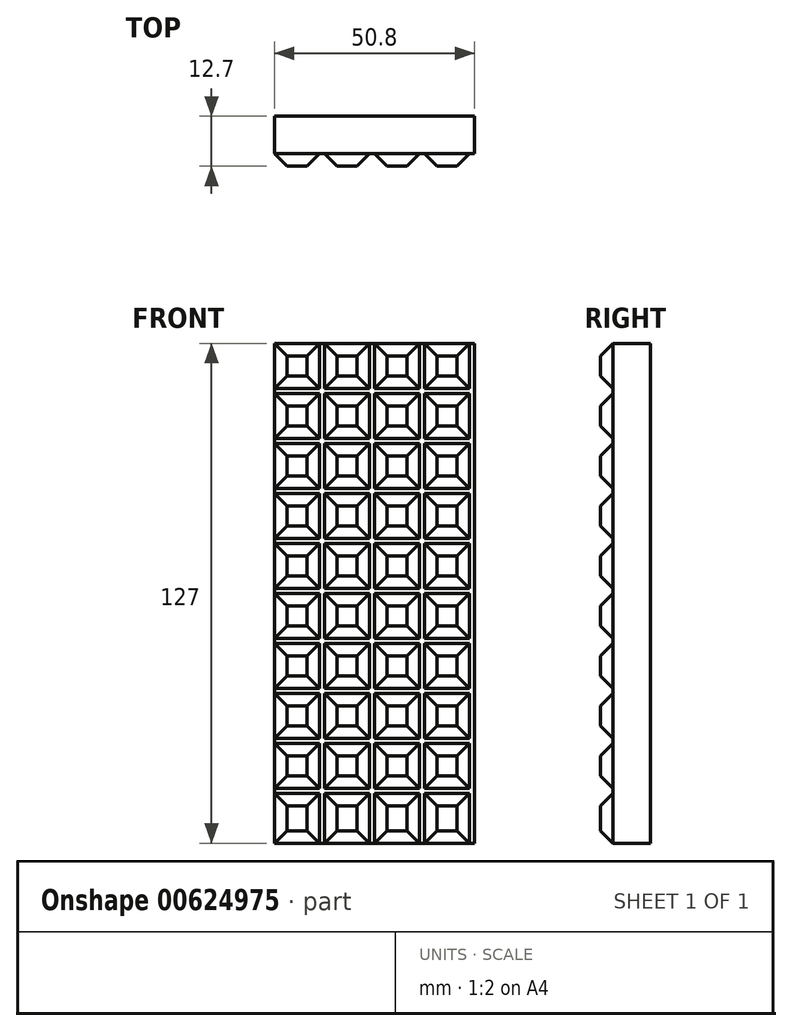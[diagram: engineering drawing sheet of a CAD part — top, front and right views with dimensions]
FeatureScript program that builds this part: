
annotation { "Feature Type Name" : "Feature", "Feature Type Description" : "" }
export const myFeature = defineFeature(function(context is Context, id is Id, definition is map)
    precondition{}
    {
        {
            var Q0;
            Q0=qCreatedBy(makeId("Front.planeOp"),FACE);
            var sketch = newSketch(context, id + "F0", { "sketchPlane" : qUnion([Q0])});
            skLineSegment(sketch, "E0.bottom", {"start": v(0, 0) * mm, "end": v(50.8, 0) * mm});
            skLineSegment(sketch, "E0.top", {"start": v(0, 127) * mm, "end": v(50.8, 127) * mm});
            skLineSegment(sketch, "E0.left", {"start": v(0, 0) * mm, "end": v(0, 127) * mm});
            skLineSegment(sketch, "E0.right", {"start": v(50.8, 0) * mm, "end": v(50.8, 127) * mm});
            skSolve(sketch);
        }
        {
            var Q0;
            Q0 = qSketchRegion(id + "F0", true);
            extrude(context, id + "F1", {"entities" : qUnion([Q0]), "depth" : 12.7 * mm, "offsetDistance" : 25.4 * mm});
        }
        {
            var Q0;
            Q0=makeQuery(id+"F1.opExtrude","CAP_FACE",FACE,{"disambiguationData":[OSD([sQuery(id+"F0.wireOp",EDGE,"E0.bottom"),sQuery(id+"F0.wireOp",EDGE,"E0.top"),sQuery(id+"F0.wireOp",EDGE,"E0.left"),sQuery(id+"F0.wireOp",EDGE,"E0.right")])],"isStart":false});
            var sketch = newSketch(context, id + "F2", { "sketchPlane" : qUnion([Q0])});
            skLineSegment(sketch, "E1", {"start": v(11.43, 0) * mm, "end": v(11.43, 12.7) * mm});
            skLineSegment(sketch, "E2", {"start": v(12.7, 127) * mm, "end": v(12.7, 115.57) * mm});
            skLineSegment(sketch, "E3.1.0.0", {"start": v(25.4, 127) * mm, "end": v(25.4, 115.57) * mm});
            skLineSegment(sketch, "E3.1.0.1", {"start": v(24.13, 0) * mm, "end": v(24.13, 12.7) * mm});
            skLineSegment(sketch, "E3.2.0.0", {"start": v(38.1, 127) * mm, "end": v(38.1, 115.57) * mm});
            skLineSegment(sketch, "E3.2.0.1", {"start": v(36.83, 0) * mm, "end": v(36.83, 12.7) * mm});
            skLineSegment(sketch, "E3.direction1", {"start": v(11.43, 0) * mm, "end": v(24.13, 0) * mm, "construction": true});
            skLineSegment(sketch, "E4.0.3.0", {"start": v(50.8, 127) * mm, "end": v(50.8, 0) * mm});
            skLineSegment(sketch, "E4.3.3.0", {"start": v(49.53, 0) * mm, "end": v(49.53, 12.7) * mm});
            skLineSegment(sketch, "E5", {"start": v(0, 115.57) * mm, "end": v(11.43, 115.57) * mm});
            skLineSegment(sketch, "E6", {"start": v(0, 114.3) * mm, "end": v(11.43, 114.3) * mm});
            skLineSegment(sketch, "E7.0.1.0", {"start": v(0, 101.6) * mm, "end": v(11.43, 101.6) * mm});
            skLineSegment(sketch, "E7.0.1.1", {"start": v(0, 102.87) * mm, "end": v(11.43, 102.87) * mm});
            skLineSegment(sketch, "E7.0.2.0", {"start": v(0, 88.9) * mm, "end": v(11.43, 88.9) * mm});
            skLineSegment(sketch, "E7.0.2.1", {"start": v(0, 90.17) * mm, "end": v(11.43, 90.17) * mm});
            skLineSegment(sketch, "E7.0.3.0", {"start": v(0, 76.2) * mm, "end": v(11.43, 76.2) * mm});
            skLineSegment(sketch, "E7.0.3.1", {"start": v(0, 77.47) * mm, "end": v(11.43, 77.47) * mm});
            skLineSegment(sketch, "E7.0.4.0", {"start": v(0, 63.5) * mm, "end": v(11.43, 63.5) * mm});
            skLineSegment(sketch, "E7.0.4.1", {"start": v(0, 64.77) * mm, "end": v(11.43, 64.77) * mm});
            skLineSegment(sketch, "E7.0.5.0", {"start": v(0, 50.8) * mm, "end": v(11.43, 50.8) * mm});
            skLineSegment(sketch, "E7.0.5.1", {"start": v(0, 52.07) * mm, "end": v(11.43, 52.07) * mm});
            skLineSegment(sketch, "E7.0.6.0", {"start": v(0, 38.1) * mm, "end": v(11.43, 38.1) * mm});
            skLineSegment(sketch, "E7.0.6.1", {"start": v(0, 39.37) * mm, "end": v(11.43, 39.37) * mm});
            skLineSegment(sketch, "E7.0.7.0", {"start": v(0, 25.4) * mm, "end": v(11.43, 25.4) * mm});
            skLineSegment(sketch, "E7.0.7.1", {"start": v(0, 26.67) * mm, "end": v(11.43, 26.67) * mm});
            skLineSegment(sketch, "E7.0.8.0", {"start": v(0, 12.7) * mm, "end": v(11.43, 12.7) * mm});
            skLineSegment(sketch, "E7.0.8.1", {"start": v(0, 13.97) * mm, "end": v(11.43, 13.97) * mm});
            skLineSegment(sketch, "E7.0.9.0", {"start": v(0, 0) * mm, "end": v(50.8, 0) * mm});
            skLineSegment(sketch, "E7.direction1", {"start": v(0, 114.3) * mm, "end": v(-26.1, 114.3) * mm, "construction": true});
            skLineSegment(sketch, "E7.direction2", {"start": v(0, 114.3) * mm, "end": v(0, 101.6) * mm, "construction": true});
            skLineSegment(sketch, "E8", {"start": v(0, 127) * mm, "end": v(0, -127) * mm});
            skLineSegment(sketch, "E9", {"start": v(0, 127) * mm, "end": v(101.6, 127) * mm});
            skLineSegment(sketch, "E10.trimOffspring", {"start": v(12.7, 115.57) * mm, "end": v(24.13, 115.57) * mm});
            skLineSegment(sketch, "E11.trimOffspring", {"start": v(12.7, 114.3) * mm, "end": v(12.7, 102.87) * mm});
            skLineSegment(sketch, "E12.trimOffspring", {"start": v(12.7, 114.3) * mm, "end": v(24.13, 114.3) * mm});
            skLineSegment(sketch, "E13.trimOffspring", {"start": v(11.43, 115.57) * mm, "end": v(11.43, 127) * mm});
            skLineSegment(sketch, "E14.trimOffspring", {"start": v(24.13, 115.57) * mm, "end": v(24.13, 127) * mm});
            skLineSegment(sketch, "E15.trimOffspring", {"start": v(25.4, 115.57) * mm, "end": v(36.83, 115.57) * mm});
            skLineSegment(sketch, "E16.trimOffspring", {"start": v(25.4, 114.3) * mm, "end": v(25.4, 102.87) * mm});
            skLineSegment(sketch, "E17.trimOffspring", {"start": v(25.4, 114.3) * mm, "end": v(36.83, 114.3) * mm});
            skLineSegment(sketch, "E18.trimOffspring", {"start": v(38.1, 115.57) * mm, "end": v(49.53, 115.57) * mm});
            skLineSegment(sketch, "E19.trimOffspring", {"start": v(38.1, 114.3) * mm, "end": v(38.1, 102.87) * mm});
            skLineSegment(sketch, "E20.trimOffspring", {"start": v(38.1, 114.3) * mm, "end": v(49.53, 114.3) * mm});
            skLineSegment(sketch, "E21.trimOffspring", {"start": v(36.83, 115.57) * mm, "end": v(36.83, 127) * mm});
            skLineSegment(sketch, "E22.trimOffspring", {"start": v(49.53, 115.57) * mm, "end": v(49.53, 127) * mm});
            skPoint(sketch, "E23.orphan", {"position": v(50.8, 115.57) * mm});
            skPoint(sketch, "E24.orphan", {"position": v(50.8, 114.3) * mm});
            skPoint(sketch, "E25.orphan", {"position": v(50.8, 102.87) * mm});
            skLineSegment(sketch, "E26.trimOffspring", {"start": v(49.53, 102.87) * mm, "end": v(49.53, 114.3) * mm});
            skPoint(sketch, "E27.orphan", {"position": v(50.8, 101.6) * mm});
            skLineSegment(sketch, "E28.trimOffspring", {"start": v(38.1, 101.6) * mm, "end": v(38.1, 90.17) * mm});
            skLineSegment(sketch, "E29.trimOffspring", {"start": v(38.1, 102.87) * mm, "end": v(49.53, 102.87) * mm});
            skLineSegment(sketch, "E30.trimOffspring", {"start": v(36.83, 102.87) * mm, "end": v(36.83, 114.3) * mm});
            skLineSegment(sketch, "E31.trimOffspring", {"start": v(38.1, 101.6) * mm, "end": v(49.53, 101.6) * mm});
            skLineSegment(sketch, "E32.trimOffspring", {"start": v(25.4, 101.6) * mm, "end": v(25.4, 90.17) * mm});
            skLineSegment(sketch, "E33.trimOffspring", {"start": v(25.4, 102.87) * mm, "end": v(36.83, 102.87) * mm});
            skLineSegment(sketch, "E34.trimOffspring", {"start": v(24.13, 102.87) * mm, "end": v(24.13, 114.3) * mm});
            skLineSegment(sketch, "E35.trimOffspring", {"start": v(25.4, 101.6) * mm, "end": v(36.83, 101.6) * mm});
            skLineSegment(sketch, "E36.trimOffspring", {"start": v(12.7, 102.87) * mm, "end": v(24.13, 102.87) * mm});
            skLineSegment(sketch, "E37.trimOffspring", {"start": v(11.43, 102.87) * mm, "end": v(11.43, 114.3) * mm});
            skLineSegment(sketch, "E38.trimOffspring", {"start": v(12.7, 101.6) * mm, "end": v(24.13, 101.6) * mm});
            skLineSegment(sketch, "E39.trimOffspring", {"start": v(11.43, 90.17) * mm, "end": v(11.43, 101.6) * mm});
            skLineSegment(sketch, "E40.trimOffspring", {"start": v(12.7, 90.17) * mm, "end": v(24.13, 90.17) * mm});
            skLineSegment(sketch, "E41.trimOffspring", {"start": v(12.7, 88.9) * mm, "end": v(24.13, 88.9) * mm});
            skLineSegment(sketch, "E42.trimOffspring", {"start": v(12.7, 88.9) * mm, "end": v(12.7, 77.47) * mm});
            skLineSegment(sketch, "E43.trimOffspring", {"start": v(24.13, 90.17) * mm, "end": v(24.13, 101.6) * mm});
            skLineSegment(sketch, "E44.trimOffspring", {"start": v(25.4, 90.17) * mm, "end": v(36.83, 90.17) * mm});
            skLineSegment(sketch, "E45.trimOffspring", {"start": v(25.4, 88.9) * mm, "end": v(25.4, 77.47) * mm});
            skLineSegment(sketch, "E46.trimOffspring", {"start": v(25.4, 88.9) * mm, "end": v(36.83, 88.9) * mm});
            skLineSegment(sketch, "E47.trimOffspring", {"start": v(36.83, 90.17) * mm, "end": v(36.83, 101.6) * mm});
            skLineSegment(sketch, "E48.trimOffspring", {"start": v(38.1, 90.17) * mm, "end": v(49.53, 90.17) * mm});
            skLineSegment(sketch, "E49.trimOffspring", {"start": v(38.1, 88.9) * mm, "end": v(38.1, 77.47) * mm});
            skLineSegment(sketch, "E50.trimOffspring", {"start": v(38.1, 88.9) * mm, "end": v(49.53, 88.9) * mm});
            skLineSegment(sketch, "E51.trimOffspring", {"start": v(49.53, 90.17) * mm, "end": v(49.53, 101.6) * mm});
            skPoint(sketch, "E52.orphan", {"position": v(50.8, 90.17) * mm});
            skPoint(sketch, "E53.orphan", {"position": v(50.8, 88.9) * mm});
            skPoint(sketch, "E54.orphan", {"position": v(50.8, 77.47) * mm});
            skLineSegment(sketch, "E55.trimOffspring", {"start": v(49.53, 77.47) * mm, "end": v(49.53, 88.9) * mm});
            skPoint(sketch, "E56.orphan", {"position": v(50.8, 76.2) * mm});
            skLineSegment(sketch, "E57.trimOffspring", {"start": v(38.1, 76.2) * mm, "end": v(38.1, 64.77) * mm});
            skLineSegment(sketch, "E58.trimOffspring", {"start": v(38.1, 77.47) * mm, "end": v(49.53, 77.47) * mm});
            skLineSegment(sketch, "E59.trimOffspring", {"start": v(36.83, 77.47) * mm, "end": v(36.83, 88.9) * mm});
            skLineSegment(sketch, "E60.trimOffspring", {"start": v(38.1, 76.2) * mm, "end": v(49.53, 76.2) * mm});
            skLineSegment(sketch, "E61.trimOffspring", {"start": v(25.4, 76.2) * mm, "end": v(25.4, 64.77) * mm});
            skLineSegment(sketch, "E62.trimOffspring", {"start": v(25.4, 77.47) * mm, "end": v(36.83, 77.47) * mm});
            skLineSegment(sketch, "E63.trimOffspring", {"start": v(24.13, 77.47) * mm, "end": v(24.13, 88.9) * mm});
            skLineSegment(sketch, "E64.trimOffspring", {"start": v(25.4, 76.2) * mm, "end": v(36.83, 76.2) * mm});
            skLineSegment(sketch, "E65.trimOffspring", {"start": v(12.7, 76.2) * mm, "end": v(12.7, 64.77) * mm});
            skLineSegment(sketch, "E66.trimOffspring", {"start": v(11.43, 77.47) * mm, "end": v(11.43, 88.9) * mm});
            skLineSegment(sketch, "E67.trimOffspring", {"start": v(12.7, 77.47) * mm, "end": v(24.13, 77.47) * mm});
            skLineSegment(sketch, "E68.trimOffspring", {"start": v(12.7, 76.2) * mm, "end": v(24.13, 76.2) * mm});
            skLineSegment(sketch, "E69.trimOffspring", {"start": v(12.7, 64.77) * mm, "end": v(24.13, 64.77) * mm});
            skLineSegment(sketch, "E70.trimOffspring", {"start": v(12.7, 63.5) * mm, "end": v(12.7, 52.07) * mm});
            skLineSegment(sketch, "E71.trimOffspring", {"start": v(12.7, 63.5) * mm, "end": v(24.13, 63.5) * mm});
            skLineSegment(sketch, "E72.trimOffspring", {"start": v(11.43, 64.77) * mm, "end": v(11.43, 76.2) * mm});
            skLineSegment(sketch, "E73.trimOffspring", {"start": v(24.13, 64.77) * mm, "end": v(24.13, 76.2) * mm});
            skLineSegment(sketch, "E74.trimOffspring", {"start": v(25.4, 64.77) * mm, "end": v(36.83, 64.77) * mm});
            skLineSegment(sketch, "E75.trimOffspring", {"start": v(25.4, 63.5) * mm, "end": v(25.4, 52.07) * mm});
            skLineSegment(sketch, "E76.trimOffspring", {"start": v(25.4, 63.5) * mm, "end": v(36.83, 63.5) * mm});
            skLineSegment(sketch, "E77.trimOffspring", {"start": v(36.83, 64.77) * mm, "end": v(36.83, 76.2) * mm});
            skLineSegment(sketch, "E78.trimOffspring", {"start": v(38.1, 64.77) * mm, "end": v(49.53, 64.77) * mm});
            skLineSegment(sketch, "E79.trimOffspring", {"start": v(38.1, 63.5) * mm, "end": v(38.1, 52.07) * mm});
            skLineSegment(sketch, "E80.trimOffspring", {"start": v(38.1, 63.5) * mm, "end": v(49.53, 63.5) * mm});
            skLineSegment(sketch, "E81.trimOffspring", {"start": v(49.53, 64.77) * mm, "end": v(49.53, 76.2) * mm});
            skPoint(sketch, "E82.orphan", {"position": v(50.8, 64.77) * mm});
            skPoint(sketch, "E83.orphan", {"position": v(50.8, 63.5) * mm});
            skPoint(sketch, "E84.orphan", {"position": v(50.8, 52.07) * mm});
            skLineSegment(sketch, "E85.trimOffspring", {"start": v(49.53, 52.07) * mm, "end": v(49.53, 63.5) * mm});
            skPoint(sketch, "E86.orphan", {"position": v(50.8, 50.8) * mm});
            skLineSegment(sketch, "E87.trimOffspring", {"start": v(38.1, 50.8) * mm, "end": v(38.1, 39.37) * mm});
            skLineSegment(sketch, "E88.trimOffspring", {"start": v(38.1, 52.07) * mm, "end": v(49.53, 52.07) * mm});
            skLineSegment(sketch, "E89.trimOffspring", {"start": v(36.83, 52.07) * mm, "end": v(36.83, 63.5) * mm});
            skLineSegment(sketch, "E90.trimOffspring", {"start": v(38.1, 50.8) * mm, "end": v(49.53, 50.8) * mm});
            skLineSegment(sketch, "E91.trimOffspring", {"start": v(25.4, 50.8) * mm, "end": v(25.4, 39.37) * mm});
            skLineSegment(sketch, "E92.trimOffspring", {"start": v(25.4, 52.07) * mm, "end": v(36.83, 52.07) * mm});
            skLineSegment(sketch, "E93.trimOffspring", {"start": v(24.13, 52.07) * mm, "end": v(24.13, 63.5) * mm});
            skLineSegment(sketch, "E94.trimOffspring", {"start": v(25.4, 50.8) * mm, "end": v(36.83, 50.8) * mm});
            skLineSegment(sketch, "E95.trimOffspring", {"start": v(12.7, 50.8) * mm, "end": v(12.7, 39.37) * mm});
            skLineSegment(sketch, "E96.trimOffspring", {"start": v(12.7, 52.07) * mm, "end": v(24.13, 52.07) * mm});
            skLineSegment(sketch, "E97.trimOffspring", {"start": v(11.43, 52.07) * mm, "end": v(11.43, 63.5) * mm});
            skLineSegment(sketch, "E98.trimOffspring", {"start": v(12.7, 50.8) * mm, "end": v(24.13, 50.8) * mm});
            skLineSegment(sketch, "E99.trimOffspring", {"start": v(12.7, 39.37) * mm, "end": v(24.13, 39.37) * mm});
            skLineSegment(sketch, "E100.trimOffspring", {"start": v(12.7, 38.1) * mm, "end": v(12.7, 26.67) * mm});
            skLineSegment(sketch, "E101.trimOffspring", {"start": v(12.7, 38.1) * mm, "end": v(24.13, 38.1) * mm});
            skLineSegment(sketch, "E102.trimOffspring", {"start": v(11.43, 39.37) * mm, "end": v(11.43, 50.8) * mm});
            skLineSegment(sketch, "E103.trimOffspring", {"start": v(24.13, 39.37) * mm, "end": v(24.13, 50.8) * mm});
            skLineSegment(sketch, "E104.trimOffspring", {"start": v(25.4, 39.37) * mm, "end": v(36.83, 39.37) * mm});
            skLineSegment(sketch, "E105.trimOffspring", {"start": v(25.4, 38.1) * mm, "end": v(25.4, 26.67) * mm});
            skLineSegment(sketch, "E106.trimOffspring", {"start": v(25.4, 38.1) * mm, "end": v(36.83, 38.1) * mm});
            skLineSegment(sketch, "E107.trimOffspring", {"start": v(36.83, 39.37) * mm, "end": v(36.83, 50.8) * mm});
            skLineSegment(sketch, "E108.trimOffspring", {"start": v(38.1, 39.37) * mm, "end": v(49.53, 39.37) * mm});
            skLineSegment(sketch, "E109.trimOffspring", {"start": v(38.1, 38.1) * mm, "end": v(38.1, 26.67) * mm});
            skLineSegment(sketch, "E110.trimOffspring", {"start": v(38.1, 38.1) * mm, "end": v(49.53, 38.1) * mm});
            skLineSegment(sketch, "E111.trimOffspring", {"start": v(49.53, 39.37) * mm, "end": v(49.53, 50.8) * mm});
            skPoint(sketch, "E112.orphan", {"position": v(50.8, 39.37) * mm});
            skPoint(sketch, "E113.orphan", {"position": v(50.8, 38.1) * mm});
            skPoint(sketch, "E114.orphan", {"position": v(50.8, 26.67) * mm});
            skPoint(sketch, "E115.orphan", {"position": v(50.8, 25.4) * mm});
            skLineSegment(sketch, "E116.trimOffspring", {"start": v(49.53, 26.67) * mm, "end": v(49.53, 38.1) * mm});
            skLineSegment(sketch, "E117.trimOffspring", {"start": v(38.1, 25.4) * mm, "end": v(38.1, 13.97) * mm});
            skLineSegment(sketch, "E118.trimOffspring", {"start": v(38.1, 26.67) * mm, "end": v(49.53, 26.67) * mm});
            skLineSegment(sketch, "E119.trimOffspring", {"start": v(36.83, 26.67) * mm, "end": v(36.83, 38.1) * mm});
            skLineSegment(sketch, "E120.trimOffspring", {"start": v(38.1, 25.4) * mm, "end": v(49.53, 25.4) * mm});
            skLineSegment(sketch, "E121.trimOffspring", {"start": v(25.4, 25.4) * mm, "end": v(25.4, 13.97) * mm});
            skLineSegment(sketch, "E122.trimOffspring", {"start": v(25.4, 26.67) * mm, "end": v(36.83, 26.67) * mm});
            skLineSegment(sketch, "E123.trimOffspring", {"start": v(24.13, 26.67) * mm, "end": v(24.13, 38.1) * mm});
            skLineSegment(sketch, "E124.trimOffspring", {"start": v(25.4, 25.4) * mm, "end": v(36.83, 25.4) * mm});
            skLineSegment(sketch, "E125.trimOffspring", {"start": v(12.7, 25.4) * mm, "end": v(12.7, 13.97) * mm});
            skLineSegment(sketch, "E126.trimOffspring", {"start": v(12.7, 26.67) * mm, "end": v(24.13, 26.67) * mm});
            skLineSegment(sketch, "E127.trimOffspring", {"start": v(11.43, 26.67) * mm, "end": v(11.43, 38.1) * mm});
            skLineSegment(sketch, "E128.trimOffspring", {"start": v(12.7, 25.4) * mm, "end": v(24.13, 25.4) * mm});
            skLineSegment(sketch, "E129.trimOffspring", {"start": v(12.7, 13.97) * mm, "end": v(24.13, 13.97) * mm});
            skLineSegment(sketch, "E130.trimOffspring", {"start": v(11.43, 13.97) * mm, "end": v(11.43, 25.4) * mm});
            skLineSegment(sketch, "E131.trimOffspring", {"start": v(12.7, 12.7) * mm, "end": v(12.7, 0) * mm});
            skLineSegment(sketch, "E132.trimOffspring", {"start": v(12.7, 12.7) * mm, "end": v(24.13, 12.7) * mm});
            skLineSegment(sketch, "E133.trimOffspring", {"start": v(24.13, 13.97) * mm, "end": v(24.13, 25.4) * mm});
            skLineSegment(sketch, "E134.trimOffspring", {"start": v(25.4, 13.97) * mm, "end": v(36.83, 13.97) * mm});
            skLineSegment(sketch, "E135.trimOffspring", {"start": v(25.4, 12.7) * mm, "end": v(25.4, 0) * mm});
            skLineSegment(sketch, "E136.trimOffspring", {"start": v(25.4, 12.7) * mm, "end": v(36.83, 12.7) * mm});
            skLineSegment(sketch, "E137.trimOffspring", {"start": v(36.83, 13.97) * mm, "end": v(36.83, 25.4) * mm});
            skLineSegment(sketch, "E138.trimOffspring", {"start": v(38.1, 13.97) * mm, "end": v(49.53, 13.97) * mm});
            skLineSegment(sketch, "E139.trimOffspring", {"start": v(38.1, 12.7) * mm, "end": v(38.1, 0) * mm});
            skLineSegment(sketch, "E140.trimOffspring", {"start": v(38.1, 12.7) * mm, "end": v(49.53, 12.7) * mm});
            skLineSegment(sketch, "E141.trimOffspring", {"start": v(49.53, 13.97) * mm, "end": v(49.53, 25.4) * mm});
            skPoint(sketch, "E142.orphan", {"position": v(50.8, 13.97) * mm});
            skPoint(sketch, "E143.orphan", {"position": v(50.8, 12.7) * mm});
            skPoint(sketch, "E144.orphan", {"position": v(50.8, 1.27) * mm});
            skLineSegment(sketch, "E145", {"start": v(12.7, 101.6) * mm, "end": v(12.7, 90.17) * mm});
            skSolve(sketch);
        }
        {
            var Q0;
            {var subQ23=sQuery(id+"F2.wireOp",EDGE,"E1");Q0=makeQuery(id+"F2.imprint","IMPRINT",FACE,{"disambiguationData":[TD([[makeQuery(id+"F2.imprint","IMPRINT",EDGE,{"derivedFrom":subQ23}),-1.0]])]});}
            extrude(context, id + "F3", {"entities" : qUnion([Q0]), "operationType" : NewBodyOperationType.REMOVE, "oppositeDirection" : true, "depth" : 3.17 * mm, "offsetDistance" : 25.4 * mm});
        }
        {
            var Q0;
            Q0=makeQuery(id+"F3.boolean.opBoolean","COPY",EDGE,{"derivedFrom":makeQuery(id+"F3.opExtrude","CAP_EDGE",EDGE,{"disambiguationData":[OSD([sQuery(id+"F2.wireOp",EDGE,"E1")])],"isStart":true})});
            var Q1;
            Q1=makeQuery(id+"F3.boolean.opBoolean","COPY",EDGE,{"derivedFrom":makeQuery(id+"F3.opExtrude","CAP_EDGE",EDGE,{"disambiguationData":[OSD([sQuery(id+"F2.wireOp",EDGE,"E7.0.8.0")])],"isStart":true})});
            var Q2;
            Q2=makeQuery(id+"F3.boolean.opBoolean","COPY",EDGE,{"derivedFrom":makeQuery(id+"F3.opExtrude","CAP_EDGE",EDGE,{"disambiguationData":[OSD([sQuery(id+"F2.wireOp",EDGE,"E132.trimOffspring")])],"isStart":true})});
            var Q3;
            Q3=makeQuery(id+"F3.boolean.opBoolean","COPY",EDGE,{"derivedFrom":makeQuery(id+"F3.opExtrude","CAP_EDGE",EDGE,{"disambiguationData":[OSD([sQuery(id+"F2.wireOp",EDGE,"E131.trimOffspring")])],"isStart":true})});
            var Q4;
            Q4=makeQuery(id+"F3.boolean.opBoolean","COPY",EDGE,{"derivedFrom":makeQuery(id+"F3.opExtrude","CAP_EDGE",EDGE,{"disambiguationData":[OSD([sQuery(id+"F2.wireOp",EDGE,"E3.1.0.1")])],"isStart":true})});
            var Q5;
            Q5=makeQuery(id+"F3.boolean.opBoolean","COPY",EDGE,{"derivedFrom":makeQuery(id+"F3.opExtrude","CAP_EDGE",EDGE,{"disambiguationData":[OSD([sQuery(id+"F2.wireOp",EDGE,"E136.trimOffspring")])],"isStart":true})});
            var Q6;
            Q6=makeQuery(id+"F3.boolean.opBoolean","COPY",EDGE,{"derivedFrom":makeQuery(id+"F3.opExtrude","CAP_EDGE",EDGE,{"disambiguationData":[OSD([sQuery(id+"F2.wireOp",EDGE,"E135.trimOffspring")])],"isStart":true})});
            var Q7;
            Q7=makeQuery(id+"F3.boolean.opBoolean","COPY",EDGE,{"derivedFrom":makeQuery(id+"F3.opExtrude","CAP_EDGE",EDGE,{"disambiguationData":[OSD([sQuery(id+"F2.wireOp",EDGE,"E3.2.0.1")])],"isStart":true})});
            var Q8;
            Q8=makeQuery(id+"F3.boolean.opBoolean","COPY",EDGE,{"derivedFrom":makeQuery(id+"F3.opExtrude","CAP_EDGE",EDGE,{"disambiguationData":[OSD([sQuery(id+"F2.wireOp",EDGE,"E139.trimOffspring")])],"isStart":true})});
            var Q9;
            Q9=makeQuery(id+"F3.boolean.opBoolean","COPY",EDGE,{"derivedFrom":makeQuery(id+"F3.opExtrude","CAP_EDGE",EDGE,{"disambiguationData":[OSD([sQuery(id+"F2.wireOp",EDGE,"E140.trimOffspring")])],"isStart":true})});
            var Q10;
            Q10=makeQuery(id+"F3.boolean.opBoolean","COPY",EDGE,{"derivedFrom":makeQuery(id+"F3.opExtrude","CAP_EDGE",EDGE,{"disambiguationData":[OSD([sQuery(id+"F2.wireOp",EDGE,"E138.trimOffspring")])],"isStart":true})});
            var Q11;
            Q11=makeQuery(id+"F3.boolean.opBoolean","COPY",EDGE,{"derivedFrom":makeQuery(id+"F3.opExtrude","CAP_EDGE",EDGE,{"disambiguationData":[OSD([sQuery(id+"F2.wireOp",EDGE,"E117.trimOffspring")])],"isStart":true})});
            var Q12;
            Q12=makeQuery(id+"F3.boolean.opBoolean","COPY",EDGE,{"derivedFrom":makeQuery(id+"F3.opExtrude","CAP_EDGE",EDGE,{"disambiguationData":[OSD([sQuery(id+"F2.wireOp",EDGE,"E120.trimOffspring")])],"isStart":true})});
            var Q13;
            Q13=makeQuery(id+"F3.boolean.opBoolean","COPY",EDGE,{"derivedFrom":makeQuery(id+"F3.opExtrude","CAP_EDGE",EDGE,{"disambiguationData":[OSD([sQuery(id+"F2.wireOp",EDGE,"E137.trimOffspring")])],"isStart":true})});
            var Q14;
            Q14=makeQuery(id+"F3.boolean.opBoolean","SPLIT",FACE,{"disambiguationData":[TD([makeQuery(id+"F3.opExtrude","SWEPT_FACE",FACE,{"disambiguationData":[OSD([sQuery(id+"F2.wireOp",EDGE,"E125.trimOffspring")])]})])],"derivedFrom":makeQuery(id+"F1.opExtrude","CAP_FACE",FACE,{"disambiguationData":[OSD([sQuery(id+"F0.wireOp",EDGE,"E0.bottom"),sQuery(id+"F0.wireOp",EDGE,"E0.top"),sQuery(id+"F0.wireOp",EDGE,"E0.left"),sQuery(id+"F0.wireOp",EDGE,"E0.right")])],"isStart":false})});
            var Q15;
            Q15=makeQuery(id+"F3.boolean.opBoolean","SPLIT",FACE,{"disambiguationData":[TD([makeQuery(id+"F3.opExtrude","SWEPT_FACE",FACE,{"disambiguationData":[OSD([sQuery(id+"F2.wireOp",EDGE,"E105.trimOffspring")])]})])],"derivedFrom":makeQuery(id+"F1.opExtrude","CAP_FACE",FACE,{"disambiguationData":[OSD([sQuery(id+"F0.wireOp",EDGE,"E0.bottom"),sQuery(id+"F0.wireOp",EDGE,"E0.top"),sQuery(id+"F0.wireOp",EDGE,"E0.left"),sQuery(id+"F0.wireOp",EDGE,"E0.right")])],"isStart":false})});
            var Q16;
            Q16=makeQuery(id+"F3.boolean.opBoolean","SPLIT",FACE,{"disambiguationData":[TD([makeQuery(id+"F3.opExtrude","SWEPT_FACE",FACE,{"disambiguationData":[OSD([sQuery(id+"F2.wireOp",EDGE,"E100.trimOffspring")])]})])],"derivedFrom":makeQuery(id+"F1.opExtrude","CAP_FACE",FACE,{"disambiguationData":[OSD([sQuery(id+"F0.wireOp",EDGE,"E0.bottom"),sQuery(id+"F0.wireOp",EDGE,"E0.top"),sQuery(id+"F0.wireOp",EDGE,"E0.left"),sQuery(id+"F0.wireOp",EDGE,"E0.right")])],"isStart":false})});
            var Q17;
            Q17=makeQuery(id+"F3.boolean.opBoolean","COPY",EDGE,{"derivedFrom":makeQuery(id+"F3.opExtrude","CAP_EDGE",EDGE,{"disambiguationData":[OSD([sQuery(id+"F2.wireOp",EDGE,"E124.trimOffspring")])],"isStart":true})});
            var Q18;
            Q18=makeQuery(id+"F3.boolean.opBoolean","COPY",EDGE,{"derivedFrom":makeQuery(id+"F3.opExtrude","CAP_EDGE",EDGE,{"disambiguationData":[OSD([sQuery(id+"F2.wireOp",EDGE,"E121.trimOffspring")])],"isStart":true})});
            var Q19;
            Q19=makeQuery(id+"F3.boolean.opBoolean","SPLIT",FACE,{"disambiguationData":[TD([makeQuery(id+"F3.opExtrude","SWEPT_FACE",FACE,{"disambiguationData":[OSD([sQuery(id+"F2.wireOp",EDGE,"E121.trimOffspring")])]})])],"derivedFrom":makeQuery(id+"F1.opExtrude","CAP_FACE",FACE,{"disambiguationData":[OSD([sQuery(id+"F0.wireOp",EDGE,"E0.bottom"),sQuery(id+"F0.wireOp",EDGE,"E0.top"),sQuery(id+"F0.wireOp",EDGE,"E0.left"),sQuery(id+"F0.wireOp",EDGE,"E0.right")])],"isStart":false})});
            var Q20;
            Q20=makeQuery(id+"F3.boolean.opBoolean","SPLIT",FACE,{"disambiguationData":[TD([makeQuery(id+"F3.opExtrude","SWEPT_FACE",FACE,{"disambiguationData":[OSD([sQuery(id+"F2.wireOp",EDGE,"E91.trimOffspring")])]})])],"derivedFrom":makeQuery(id+"F1.opExtrude","CAP_FACE",FACE,{"disambiguationData":[OSD([sQuery(id+"F0.wireOp",EDGE,"E0.bottom"),sQuery(id+"F0.wireOp",EDGE,"E0.top"),sQuery(id+"F0.wireOp",EDGE,"E0.left"),sQuery(id+"F0.wireOp",EDGE,"E0.right")])],"isStart":false})});
            var Q21;
            Q21=makeQuery(id+"F3.boolean.opBoolean","SPLIT",FACE,{"disambiguationData":[TD([makeQuery(id+"F3.opExtrude","SWEPT_FACE",FACE,{"disambiguationData":[OSD([sQuery(id+"F2.wireOp",EDGE,"E95.trimOffspring")])]})])],"derivedFrom":makeQuery(id+"F1.opExtrude","CAP_FACE",FACE,{"disambiguationData":[OSD([sQuery(id+"F0.wireOp",EDGE,"E0.bottom"),sQuery(id+"F0.wireOp",EDGE,"E0.top"),sQuery(id+"F0.wireOp",EDGE,"E0.left"),sQuery(id+"F0.wireOp",EDGE,"E0.right")])],"isStart":false})});
            var Q22;
            Q22=makeQuery(id+"F3.boolean.opBoolean","SPLIT",FACE,{"disambiguationData":[TD([makeQuery(id+"F3.opExtrude","SWEPT_FACE",FACE,{"disambiguationData":[OSD([sQuery(id+"F2.wireOp",EDGE,"E70.trimOffspring")])]})])],"derivedFrom":makeQuery(id+"F1.opExtrude","CAP_FACE",FACE,{"disambiguationData":[OSD([sQuery(id+"F0.wireOp",EDGE,"E0.bottom"),sQuery(id+"F0.wireOp",EDGE,"E0.top"),sQuery(id+"F0.wireOp",EDGE,"E0.left"),sQuery(id+"F0.wireOp",EDGE,"E0.right")])],"isStart":false})});
            var Q23;
            Q23=makeQuery(id+"F3.boolean.opBoolean","SPLIT",FACE,{"disambiguationData":[TD([makeQuery(id+"F3.opExtrude","SWEPT_FACE",FACE,{"disambiguationData":[OSD([sQuery(id+"F2.wireOp",EDGE,"E75.trimOffspring")])]})])],"derivedFrom":makeQuery(id+"F1.opExtrude","CAP_FACE",FACE,{"disambiguationData":[OSD([sQuery(id+"F0.wireOp",EDGE,"E0.bottom"),sQuery(id+"F0.wireOp",EDGE,"E0.top"),sQuery(id+"F0.wireOp",EDGE,"E0.left"),sQuery(id+"F0.wireOp",EDGE,"E0.right")])],"isStart":false})});
            var Q24;
            Q24=makeQuery(id+"F3.boolean.opBoolean","SPLIT",FACE,{"disambiguationData":[TD([makeQuery(id+"F3.opExtrude","SWEPT_FACE",FACE,{"disambiguationData":[OSD([sQuery(id+"F2.wireOp",EDGE,"E45.trimOffspring")])]})])],"derivedFrom":makeQuery(id+"F1.opExtrude","CAP_FACE",FACE,{"disambiguationData":[OSD([sQuery(id+"F0.wireOp",EDGE,"E0.bottom"),sQuery(id+"F0.wireOp",EDGE,"E0.top"),sQuery(id+"F0.wireOp",EDGE,"E0.left"),sQuery(id+"F0.wireOp",EDGE,"E0.right")])],"isStart":false})});
            var Q25;
            Q25=makeQuery(id+"F3.boolean.opBoolean","SPLIT",FACE,{"disambiguationData":[TD([makeQuery(id+"F3.opExtrude","SWEPT_FACE",FACE,{"disambiguationData":[OSD([sQuery(id+"F2.wireOp",EDGE,"E41.trimOffspring")])]})])],"derivedFrom":makeQuery(id+"F1.opExtrude","CAP_FACE",FACE,{"disambiguationData":[OSD([sQuery(id+"F0.wireOp",EDGE,"E0.bottom"),sQuery(id+"F0.wireOp",EDGE,"E0.top"),sQuery(id+"F0.wireOp",EDGE,"E0.left"),sQuery(id+"F0.wireOp",EDGE,"E0.right")])],"isStart":false})});
            var Q26;
            Q26=makeQuery(id+"F3.boolean.opBoolean","SPLIT",FACE,{"disambiguationData":[TD([makeQuery(id+"F3.opExtrude","SWEPT_FACE",FACE,{"disambiguationData":[OSD([sQuery(id+"F2.wireOp",EDGE,"E61.trimOffspring")])]})])],"derivedFrom":makeQuery(id+"F1.opExtrude","CAP_FACE",FACE,{"disambiguationData":[OSD([sQuery(id+"F0.wireOp",EDGE,"E0.bottom"),sQuery(id+"F0.wireOp",EDGE,"E0.top"),sQuery(id+"F0.wireOp",EDGE,"E0.left"),sQuery(id+"F0.wireOp",EDGE,"E0.right")])],"isStart":false})});
            var Q27;
            Q27=makeQuery(id+"F3.boolean.opBoolean","SPLIT",FACE,{"disambiguationData":[TD([makeQuery(id+"F3.opExtrude","SWEPT_FACE",FACE,{"disambiguationData":[OSD([sQuery(id+"F2.wireOp",EDGE,"E65.trimOffspring")])]})])],"derivedFrom":makeQuery(id+"F1.opExtrude","CAP_FACE",FACE,{"disambiguationData":[OSD([sQuery(id+"F0.wireOp",EDGE,"E0.bottom"),sQuery(id+"F0.wireOp",EDGE,"E0.top"),sQuery(id+"F0.wireOp",EDGE,"E0.left"),sQuery(id+"F0.wireOp",EDGE,"E0.right")])],"isStart":false})});
            var Q28;
            Q28=makeQuery(id+"F3.boolean.opBoolean","SPLIT",FACE,{"disambiguationData":[TD([makeQuery(id+"F3.opExtrude","SWEPT_FACE",FACE,{"disambiguationData":[OSD([sQuery(id+"F2.wireOp",EDGE,"E38.trimOffspring")])]})])],"derivedFrom":makeQuery(id+"F1.opExtrude","CAP_FACE",FACE,{"disambiguationData":[OSD([sQuery(id+"F0.wireOp",EDGE,"E0.bottom"),sQuery(id+"F0.wireOp",EDGE,"E0.top"),sQuery(id+"F0.wireOp",EDGE,"E0.left"),sQuery(id+"F0.wireOp",EDGE,"E0.right")])],"isStart":false})});
            var Q29;
            Q29=makeQuery(id+"F3.boolean.opBoolean","SPLIT",FACE,{"disambiguationData":[TD([makeQuery(id+"F3.opExtrude","SWEPT_FACE",FACE,{"disambiguationData":[OSD([sQuery(id+"F2.wireOp",EDGE,"E32.trimOffspring")])]})])],"derivedFrom":makeQuery(id+"F1.opExtrude","CAP_FACE",FACE,{"disambiguationData":[OSD([sQuery(id+"F0.wireOp",EDGE,"E0.bottom"),sQuery(id+"F0.wireOp",EDGE,"E0.top"),sQuery(id+"F0.wireOp",EDGE,"E0.left"),sQuery(id+"F0.wireOp",EDGE,"E0.right")])],"isStart":false})});
            var Q30;
            Q30=makeQuery(id+"F3.boolean.opBoolean","SPLIT",FACE,{"disambiguationData":[TD([makeQuery(id+"F3.opExtrude","SWEPT_FACE",FACE,{"disambiguationData":[OSD([sQuery(id+"F2.wireOp",EDGE,"E11.trimOffspring")])]})])],"derivedFrom":makeQuery(id+"F1.opExtrude","CAP_FACE",FACE,{"disambiguationData":[OSD([sQuery(id+"F0.wireOp",EDGE,"E0.bottom"),sQuery(id+"F0.wireOp",EDGE,"E0.top"),sQuery(id+"F0.wireOp",EDGE,"E0.left"),sQuery(id+"F0.wireOp",EDGE,"E0.right")])],"isStart":false})});
            var Q31;
            Q31=makeQuery(id+"F3.boolean.opBoolean","SPLIT",FACE,{"disambiguationData":[TD([makeQuery(id+"F3.opExtrude","SWEPT_FACE",FACE,{"disambiguationData":[OSD([sQuery(id+"F2.wireOp",EDGE,"E16.trimOffspring")])]})])],"derivedFrom":makeQuery(id+"F1.opExtrude","CAP_FACE",FACE,{"disambiguationData":[OSD([sQuery(id+"F0.wireOp",EDGE,"E0.bottom"),sQuery(id+"F0.wireOp",EDGE,"E0.top"),sQuery(id+"F0.wireOp",EDGE,"E0.left"),sQuery(id+"F0.wireOp",EDGE,"E0.right")])],"isStart":false})});
            var Q32;
            Q32=makeQuery(id+"F3.boolean.opBoolean","COPY",EDGE,{"derivedFrom":makeQuery(id+"F3.opExtrude","CAP_EDGE",EDGE,{"disambiguationData":[OSD([sQuery(id+"F2.wireOp",EDGE,"E130.trimOffspring")])],"isStart":true})});
            var Q33;
            Q33=makeQuery(id+"F3.boolean.opBoolean","COPY",EDGE,{"derivedFrom":makeQuery(id+"F3.opExtrude","CAP_EDGE",EDGE,{"disambiguationData":[OSD([sQuery(id+"F2.wireOp",EDGE,"E7.0.7.0")])],"isStart":true})});
            var Q34;
            Q34=makeQuery(id+"F3.boolean.opBoolean","COPY",EDGE,{"derivedFrom":makeQuery(id+"F3.opExtrude","CAP_EDGE",EDGE,{"disambiguationData":[OSD([sQuery(id+"F2.wireOp",EDGE,"E7.0.8.1")])],"isStart":true})});
            var Q35;
            Q35=makeQuery(id+"F3.boolean.opBoolean","COPY",EDGE,{"derivedFrom":makeQuery(id+"F3.opExtrude","CAP_EDGE",EDGE,{"disambiguationData":[OSD([sQuery(id+"F2.wireOp",EDGE,"E7.0.7.1")])],"isStart":true})});
            var Q36;
            Q36=makeQuery(id+"F3.boolean.opBoolean","COPY",EDGE,{"derivedFrom":makeQuery(id+"F3.opExtrude","CAP_EDGE",EDGE,{"disambiguationData":[OSD([sQuery(id+"F2.wireOp",EDGE,"E127.trimOffspring")])],"isStart":true})});
            var Q37;
            Q37=makeQuery(id+"F3.boolean.opBoolean","COPY",EDGE,{"derivedFrom":makeQuery(id+"F3.opExtrude","CAP_EDGE",EDGE,{"disambiguationData":[OSD([sQuery(id+"F2.wireOp",EDGE,"E7.0.6.0")])],"isStart":true})});
            var Q38;
            Q38=makeQuery(id+"F3.boolean.opBoolean","COPY",EDGE,{"derivedFrom":makeQuery(id+"F3.opExtrude","CAP_EDGE",EDGE,{"disambiguationData":[OSD([sQuery(id+"F2.wireOp",EDGE,"E7.0.6.1")])],"isStart":true})});
            var Q39;
            Q39=makeQuery(id+"F3.boolean.opBoolean","COPY",EDGE,{"derivedFrom":makeQuery(id+"F3.opExtrude","CAP_EDGE",EDGE,{"disambiguationData":[OSD([sQuery(id+"F2.wireOp",EDGE,"E102.trimOffspring")])],"isStart":true})});
            var Q40;
            Q40=makeQuery(id+"F3.boolean.opBoolean","COPY",EDGE,{"derivedFrom":makeQuery(id+"F3.opExtrude","CAP_EDGE",EDGE,{"disambiguationData":[OSD([sQuery(id+"F2.wireOp",EDGE,"E7.0.5.0")])],"isStart":true})});
            var Q41;
            Q41=makeQuery(id+"F3.boolean.opBoolean","COPY",EDGE,{"derivedFrom":makeQuery(id+"F3.opExtrude","CAP_EDGE",EDGE,{"disambiguationData":[OSD([sQuery(id+"F2.wireOp",EDGE,"E7.0.5.1")])],"isStart":true})});
            var Q42;
            Q42=makeQuery(id+"F3.boolean.opBoolean","COPY",EDGE,{"derivedFrom":makeQuery(id+"F3.opExtrude","CAP_EDGE",EDGE,{"disambiguationData":[OSD([sQuery(id+"F2.wireOp",EDGE,"E97.trimOffspring")])],"isStart":true})});
            var Q43;
            Q43=makeQuery(id+"F3.boolean.opBoolean","COPY",EDGE,{"derivedFrom":makeQuery(id+"F3.opExtrude","CAP_EDGE",EDGE,{"disambiguationData":[OSD([sQuery(id+"F2.wireOp",EDGE,"E7.0.4.0")])],"isStart":true})});
            var Q44;
            Q44=makeQuery(id+"F3.boolean.opBoolean","COPY",EDGE,{"derivedFrom":makeQuery(id+"F3.opExtrude","CAP_EDGE",EDGE,{"disambiguationData":[OSD([sQuery(id+"F2.wireOp",EDGE,"E7.0.4.1")])],"isStart":true})});
            var Q45;
            Q45=makeQuery(id+"F3.boolean.opBoolean","COPY",EDGE,{"derivedFrom":makeQuery(id+"F3.opExtrude","CAP_EDGE",EDGE,{"disambiguationData":[OSD([sQuery(id+"F2.wireOp",EDGE,"E72.trimOffspring")])],"isStart":true})});
            var Q46;
            Q46=makeQuery(id+"F3.boolean.opBoolean","COPY",EDGE,{"derivedFrom":makeQuery(id+"F3.opExtrude","CAP_EDGE",EDGE,{"disambiguationData":[OSD([sQuery(id+"F2.wireOp",EDGE,"E7.0.3.0")])],"isStart":true})});
            var Q47;
            Q47=makeQuery(id+"F3.boolean.opBoolean","COPY",EDGE,{"derivedFrom":makeQuery(id+"F3.opExtrude","CAP_EDGE",EDGE,{"disambiguationData":[OSD([sQuery(id+"F2.wireOp",EDGE,"E7.0.3.1")])],"isStart":true})});
            var Q48;
            Q48=makeQuery(id+"F3.boolean.opBoolean","COPY",EDGE,{"derivedFrom":makeQuery(id+"F3.opExtrude","CAP_EDGE",EDGE,{"disambiguationData":[OSD([sQuery(id+"F2.wireOp",EDGE,"E66.trimOffspring")])],"isStart":true})});
            var Q49;
            Q49=makeQuery(id+"F3.boolean.opBoolean","COPY",EDGE,{"derivedFrom":makeQuery(id+"F3.opExtrude","CAP_EDGE",EDGE,{"disambiguationData":[OSD([sQuery(id+"F2.wireOp",EDGE,"E7.0.2.0")])],"isStart":true})});
            var Q50;
            Q50=makeQuery(id+"F3.boolean.opBoolean","COPY",EDGE,{"derivedFrom":makeQuery(id+"F3.opExtrude","CAP_EDGE",EDGE,{"disambiguationData":[OSD([sQuery(id+"F2.wireOp",EDGE,"E7.0.2.1")])],"isStart":true})});
            var Q51;
            Q51=makeQuery(id+"F3.boolean.opBoolean","COPY",EDGE,{"derivedFrom":makeQuery(id+"F3.opExtrude","CAP_EDGE",EDGE,{"disambiguationData":[OSD([sQuery(id+"F2.wireOp",EDGE,"E39.trimOffspring")])],"isStart":true})});
            var Q52;
            Q52=makeQuery(id+"F3.boolean.opBoolean","COPY",EDGE,{"derivedFrom":makeQuery(id+"F3.opExtrude","CAP_EDGE",EDGE,{"disambiguationData":[OSD([sQuery(id+"F2.wireOp",EDGE,"E7.0.1.0")])],"isStart":true})});
            var Q53;
            {var subQ0=sQuery(id+"F0.wireOp",EDGE,"E0.left");Q53=makeQuery(id+"F3.boolean.opBoolean","SPLIT",FACE,{"disambiguationData":[TD([makeQuery(id+"F3.opExtrude","SWEPT_FACE",FACE,{"disambiguationData":[OSD([sQuery(id+"F2.wireOp",EDGE,"E6")])]})])],"derivedFrom":makeQuery(id+"F1.opExtrude","CAP_FACE",FACE,{"disambiguationData":[OSD([sQuery(id+"F0.wireOp",EDGE,"E0.bottom"),sQuery(id+"F0.wireOp",EDGE,"E0.top"),subQ0,sQuery(id+"F0.wireOp",EDGE,"E0.right")])],"isStart":false})});}
            var Q54;
            {var subQ0=sQuery(id+"F0.wireOp",EDGE,"E0.top");var subQ1=sQuery(id+"F0.wireOp",EDGE,"E0.left");Q54=makeQuery(id+"F3.boolean.opBoolean","SPLIT",FACE,{"disambiguationData":[TD([makeQuery(id+"F3.opExtrude","SWEPT_FACE",FACE,{"disambiguationData":[OSD([sQuery(id+"F2.wireOp",EDGE,"E5")])]})])],"derivedFrom":makeQuery(id+"F1.opExtrude","CAP_FACE",FACE,{"disambiguationData":[OSD([sQuery(id+"F0.wireOp",EDGE,"E0.bottom"),subQ0,subQ1,sQuery(id+"F0.wireOp",EDGE,"E0.right")])],"isStart":false})});}
            var Q55;
            {var subQ0=sQuery(id+"F0.wireOp",EDGE,"E0.top");Q55=makeQuery(id+"F3.boolean.opBoolean","SPLIT",FACE,{"disambiguationData":[TD([makeQuery(id+"F3.opExtrude","SWEPT_FACE",FACE,{"disambiguationData":[OSD([sQuery(id+"F2.wireOp",EDGE,"E2")])]})])],"derivedFrom":makeQuery(id+"F1.opExtrude","CAP_FACE",FACE,{"disambiguationData":[OSD([sQuery(id+"F0.wireOp",EDGE,"E0.bottom"),subQ0,sQuery(id+"F0.wireOp",EDGE,"E0.left"),sQuery(id+"F0.wireOp",EDGE,"E0.right")])],"isStart":false})});}
            var Q56;
            {var subQ0=sQuery(id+"F0.wireOp",EDGE,"E0.top");Q56=makeQuery(id+"F3.boolean.opBoolean","SPLIT",FACE,{"disambiguationData":[TD([makeQuery(id+"F3.opExtrude","SWEPT_FACE",FACE,{"disambiguationData":[OSD([sQuery(id+"F2.wireOp",EDGE,"E3.1.0.0")])]})])],"derivedFrom":makeQuery(id+"F1.opExtrude","CAP_FACE",FACE,{"disambiguationData":[OSD([sQuery(id+"F0.wireOp",EDGE,"E0.bottom"),subQ0,sQuery(id+"F0.wireOp",EDGE,"E0.left"),sQuery(id+"F0.wireOp",EDGE,"E0.right")])],"isStart":false})});}
            var Q57;
            {var subQ0=sQuery(id+"F0.wireOp",EDGE,"E0.top");Q57=makeQuery(id+"F3.boolean.opBoolean","SPLIT",FACE,{"disambiguationData":[TD([makeQuery(id+"F3.opExtrude","SWEPT_FACE",FACE,{"disambiguationData":[OSD([sQuery(id+"F2.wireOp",EDGE,"E3.2.0.0")])]})])],"derivedFrom":makeQuery(id+"F1.opExtrude","CAP_FACE",FACE,{"disambiguationData":[OSD([sQuery(id+"F0.wireOp",EDGE,"E0.bottom"),subQ0,sQuery(id+"F0.wireOp",EDGE,"E0.left"),sQuery(id+"F0.wireOp",EDGE,"E0.right")])],"isStart":false})});}
            var Q58;
            Q58=makeQuery(id+"F3.boolean.opBoolean","SPLIT",FACE,{"disambiguationData":[TD([makeQuery(id+"F3.opExtrude","SWEPT_FACE",FACE,{"disambiguationData":[OSD([sQuery(id+"F2.wireOp",EDGE,"E19.trimOffspring")])]})])],"derivedFrom":makeQuery(id+"F1.opExtrude","CAP_FACE",FACE,{"disambiguationData":[OSD([sQuery(id+"F0.wireOp",EDGE,"E0.bottom"),sQuery(id+"F0.wireOp",EDGE,"E0.top"),sQuery(id+"F0.wireOp",EDGE,"E0.left"),sQuery(id+"F0.wireOp",EDGE,"E0.right")])],"isStart":false})});
            var Q59;
            Q59=makeQuery(id+"F3.boolean.opBoolean","SPLIT",FACE,{"disambiguationData":[TD([makeQuery(id+"F3.opExtrude","SWEPT_FACE",FACE,{"disambiguationData":[OSD([sQuery(id+"F2.wireOp",EDGE,"E28.trimOffspring")])]})])],"derivedFrom":makeQuery(id+"F1.opExtrude","CAP_FACE",FACE,{"disambiguationData":[OSD([sQuery(id+"F0.wireOp",EDGE,"E0.bottom"),sQuery(id+"F0.wireOp",EDGE,"E0.top"),sQuery(id+"F0.wireOp",EDGE,"E0.left"),sQuery(id+"F0.wireOp",EDGE,"E0.right")])],"isStart":false})});
            var Q60;
            Q60=makeQuery(id+"F3.boolean.opBoolean","SPLIT",FACE,{"disambiguationData":[TD([makeQuery(id+"F3.opExtrude","SWEPT_FACE",FACE,{"disambiguationData":[OSD([sQuery(id+"F2.wireOp",EDGE,"E49.trimOffspring")])]})])],"derivedFrom":makeQuery(id+"F1.opExtrude","CAP_FACE",FACE,{"disambiguationData":[OSD([sQuery(id+"F0.wireOp",EDGE,"E0.bottom"),sQuery(id+"F0.wireOp",EDGE,"E0.top"),sQuery(id+"F0.wireOp",EDGE,"E0.left"),sQuery(id+"F0.wireOp",EDGE,"E0.right")])],"isStart":false})});
            var Q61;
            Q61=makeQuery(id+"F3.boolean.opBoolean","SPLIT",FACE,{"disambiguationData":[TD([makeQuery(id+"F3.opExtrude","SWEPT_FACE",FACE,{"disambiguationData":[OSD([sQuery(id+"F2.wireOp",EDGE,"E57.trimOffspring")])]})])],"derivedFrom":makeQuery(id+"F1.opExtrude","CAP_FACE",FACE,{"disambiguationData":[OSD([sQuery(id+"F0.wireOp",EDGE,"E0.bottom"),sQuery(id+"F0.wireOp",EDGE,"E0.top"),sQuery(id+"F0.wireOp",EDGE,"E0.left"),sQuery(id+"F0.wireOp",EDGE,"E0.right")])],"isStart":false})});
            var Q62;
            {var subQ0=sQuery(id+"F0.wireOp",EDGE,"E0.left");Q62=makeQuery(id+"F3.boolean.opBoolean","SPLIT",FACE,{"disambiguationData":[TD([makeQuery(id+"F3.opExtrude","SWEPT_FACE",FACE,{"disambiguationData":[OSD([sQuery(id+"F2.wireOp",EDGE,"E7.0.1.0")])]})])],"derivedFrom":makeQuery(id+"F1.opExtrude","CAP_FACE",FACE,{"disambiguationData":[OSD([sQuery(id+"F0.wireOp",EDGE,"E0.bottom"),sQuery(id+"F0.wireOp",EDGE,"E0.top"),subQ0,sQuery(id+"F0.wireOp",EDGE,"E0.right")])],"isStart":false})});}
            var Q63;
            {var subQ0=sQuery(id+"F0.wireOp",EDGE,"E0.left");Q63=makeQuery(id+"F3.boolean.opBoolean","SPLIT",FACE,{"disambiguationData":[TD([makeQuery(id+"F3.opExtrude","SWEPT_FACE",FACE,{"disambiguationData":[OSD([sQuery(id+"F2.wireOp",EDGE,"E7.0.2.0")])]})])],"derivedFrom":makeQuery(id+"F1.opExtrude","CAP_FACE",FACE,{"disambiguationData":[OSD([sQuery(id+"F0.wireOp",EDGE,"E0.bottom"),sQuery(id+"F0.wireOp",EDGE,"E0.top"),subQ0,sQuery(id+"F0.wireOp",EDGE,"E0.right")])],"isStart":false})});}
            var Q64;
            {var subQ0=sQuery(id+"F0.wireOp",EDGE,"E0.left");Q64=makeQuery(id+"F3.boolean.opBoolean","SPLIT",FACE,{"disambiguationData":[TD([makeQuery(id+"F3.opExtrude","SWEPT_FACE",FACE,{"disambiguationData":[OSD([sQuery(id+"F2.wireOp",EDGE,"E7.0.3.0")])]})])],"derivedFrom":makeQuery(id+"F1.opExtrude","CAP_FACE",FACE,{"disambiguationData":[OSD([sQuery(id+"F0.wireOp",EDGE,"E0.bottom"),sQuery(id+"F0.wireOp",EDGE,"E0.top"),subQ0,sQuery(id+"F0.wireOp",EDGE,"E0.right")])],"isStart":false})});}
            var Q65;
            {var subQ0=sQuery(id+"F0.wireOp",EDGE,"E0.left");Q65=makeQuery(id+"F3.boolean.opBoolean","SPLIT",FACE,{"disambiguationData":[TD([makeQuery(id+"F3.opExtrude","SWEPT_FACE",FACE,{"disambiguationData":[OSD([sQuery(id+"F2.wireOp",EDGE,"E7.0.4.0")])]})])],"derivedFrom":makeQuery(id+"F1.opExtrude","CAP_FACE",FACE,{"disambiguationData":[OSD([sQuery(id+"F0.wireOp",EDGE,"E0.bottom"),sQuery(id+"F0.wireOp",EDGE,"E0.top"),subQ0,sQuery(id+"F0.wireOp",EDGE,"E0.right")])],"isStart":false})});}
            var Q66;
            Q66=makeQuery(id+"F3.boolean.opBoolean","SPLIT",FACE,{"disambiguationData":[TD([makeQuery(id+"F3.opExtrude","SWEPT_FACE",FACE,{"disambiguationData":[OSD([sQuery(id+"F2.wireOp",EDGE,"E87.trimOffspring")])]})])],"derivedFrom":makeQuery(id+"F1.opExtrude","CAP_FACE",FACE,{"disambiguationData":[OSD([sQuery(id+"F0.wireOp",EDGE,"E0.bottom"),sQuery(id+"F0.wireOp",EDGE,"E0.top"),sQuery(id+"F0.wireOp",EDGE,"E0.left"),sQuery(id+"F0.wireOp",EDGE,"E0.right")])],"isStart":false})});
            var Q67;
            Q67=makeQuery(id+"F3.boolean.opBoolean","SPLIT",FACE,{"disambiguationData":[TD([makeQuery(id+"F3.opExtrude","SWEPT_FACE",FACE,{"disambiguationData":[OSD([sQuery(id+"F2.wireOp",EDGE,"E109.trimOffspring")])]})])],"derivedFrom":makeQuery(id+"F1.opExtrude","CAP_FACE",FACE,{"disambiguationData":[OSD([sQuery(id+"F0.wireOp",EDGE,"E0.bottom"),sQuery(id+"F0.wireOp",EDGE,"E0.top"),sQuery(id+"F0.wireOp",EDGE,"E0.left"),sQuery(id+"F0.wireOp",EDGE,"E0.right")])],"isStart":false})});
            var Q68;
            Q68=makeQuery(id+"F3.boolean.opBoolean","SPLIT",FACE,{"disambiguationData":[TD([makeQuery(id+"F3.opExtrude","SWEPT_FACE",FACE,{"disambiguationData":[OSD([sQuery(id+"F2.wireOp",EDGE,"E117.trimOffspring")])]})])],"derivedFrom":makeQuery(id+"F1.opExtrude","CAP_FACE",FACE,{"disambiguationData":[OSD([sQuery(id+"F0.wireOp",EDGE,"E0.bottom"),sQuery(id+"F0.wireOp",EDGE,"E0.top"),sQuery(id+"F0.wireOp",EDGE,"E0.left"),sQuery(id+"F0.wireOp",EDGE,"E0.right")])],"isStart":false})});
            var Q69;
            {var subQ0=sQuery(id+"F0.wireOp",EDGE,"E0.bottom");Q69=makeQuery(id+"F3.boolean.opBoolean","SPLIT",FACE,{"disambiguationData":[TD([makeQuery(id+"F3.opExtrude","SWEPT_FACE",FACE,{"disambiguationData":[OSD([sQuery(id+"F2.wireOp",EDGE,"E4.3.3.0")])]})])],"derivedFrom":makeQuery(id+"F1.opExtrude","CAP_FACE",FACE,{"disambiguationData":[OSD([subQ0,sQuery(id+"F0.wireOp",EDGE,"E0.top"),sQuery(id+"F0.wireOp",EDGE,"E0.left"),sQuery(id+"F0.wireOp",EDGE,"E0.right")])],"isStart":false})});}
            var Q70;
            {var subQ0=sQuery(id+"F0.wireOp",EDGE,"E0.bottom");Q70=makeQuery(id+"F3.boolean.opBoolean","SPLIT",FACE,{"disambiguationData":[TD([makeQuery(id+"F3.opExtrude","SWEPT_FACE",FACE,{"disambiguationData":[OSD([sQuery(id+"F2.wireOp",EDGE,"E3.2.0.1")])]})])],"derivedFrom":makeQuery(id+"F1.opExtrude","CAP_FACE",FACE,{"disambiguationData":[OSD([subQ0,sQuery(id+"F0.wireOp",EDGE,"E0.top"),sQuery(id+"F0.wireOp",EDGE,"E0.left"),sQuery(id+"F0.wireOp",EDGE,"E0.right")])],"isStart":false})});}
            var Q71;
            {var subQ0=sQuery(id+"F0.wireOp",EDGE,"E0.bottom");Q71=makeQuery(id+"F3.boolean.opBoolean","SPLIT",FACE,{"disambiguationData":[TD([makeQuery(id+"F3.opExtrude","SWEPT_FACE",FACE,{"disambiguationData":[OSD([sQuery(id+"F2.wireOp",EDGE,"E3.1.0.1")])]})])],"derivedFrom":makeQuery(id+"F1.opExtrude","CAP_FACE",FACE,{"disambiguationData":[OSD([subQ0,sQuery(id+"F0.wireOp",EDGE,"E0.top"),sQuery(id+"F0.wireOp",EDGE,"E0.left"),sQuery(id+"F0.wireOp",EDGE,"E0.right")])],"isStart":false})});}
            var Q72;
            {var subQ0=sQuery(id+"F0.wireOp",EDGE,"E0.bottom");var subQ1=sQuery(id+"F0.wireOp",EDGE,"E0.left");Q72=makeQuery(id+"F3.boolean.opBoolean","SPLIT",FACE,{"disambiguationData":[TD([makeQuery(id+"F3.opExtrude","SWEPT_FACE",FACE,{"disambiguationData":[OSD([sQuery(id+"F2.wireOp",EDGE,"E1")])]})])],"derivedFrom":makeQuery(id+"F1.opExtrude","CAP_FACE",FACE,{"disambiguationData":[OSD([subQ0,sQuery(id+"F0.wireOp",EDGE,"E0.top"),subQ1,sQuery(id+"F0.wireOp",EDGE,"E0.right")])],"isStart":false})});}
            var Q73;
            {var subQ0=sQuery(id+"F0.wireOp",EDGE,"E0.left");Q73=makeQuery(id+"F3.boolean.opBoolean","SPLIT",FACE,{"disambiguationData":[TD([makeQuery(id+"F3.opExtrude","SWEPT_FACE",FACE,{"disambiguationData":[OSD([sQuery(id+"F2.wireOp",EDGE,"E7.0.7.0")])]})])],"derivedFrom":makeQuery(id+"F1.opExtrude","CAP_FACE",FACE,{"disambiguationData":[OSD([sQuery(id+"F0.wireOp",EDGE,"E0.bottom"),sQuery(id+"F0.wireOp",EDGE,"E0.top"),subQ0,sQuery(id+"F0.wireOp",EDGE,"E0.right")])],"isStart":false})});}
            var Q74;
            {var subQ0=sQuery(id+"F0.wireOp",EDGE,"E0.left");Q74=makeQuery(id+"F3.boolean.opBoolean","SPLIT",FACE,{"disambiguationData":[TD([makeQuery(id+"F3.opExtrude","SWEPT_FACE",FACE,{"disambiguationData":[OSD([sQuery(id+"F2.wireOp",EDGE,"E7.0.6.0")])]})])],"derivedFrom":makeQuery(id+"F1.opExtrude","CAP_FACE",FACE,{"disambiguationData":[OSD([sQuery(id+"F0.wireOp",EDGE,"E0.bottom"),sQuery(id+"F0.wireOp",EDGE,"E0.top"),subQ0,sQuery(id+"F0.wireOp",EDGE,"E0.right")])],"isStart":false})});}
            var Q75;
            {var subQ0=sQuery(id+"F0.wireOp",EDGE,"E0.left");Q75=makeQuery(id+"F3.boolean.opBoolean","SPLIT",FACE,{"disambiguationData":[TD([makeQuery(id+"F3.opExtrude","SWEPT_FACE",FACE,{"disambiguationData":[OSD([sQuery(id+"F2.wireOp",EDGE,"E7.0.5.0")])]})])],"derivedFrom":makeQuery(id+"F1.opExtrude","CAP_FACE",FACE,{"disambiguationData":[OSD([sQuery(id+"F0.wireOp",EDGE,"E0.bottom"),sQuery(id+"F0.wireOp",EDGE,"E0.top"),subQ0,sQuery(id+"F0.wireOp",EDGE,"E0.right")])],"isStart":false})});}
            var Q76;
            Q76=makeQuery(id+"F3.boolean.opBoolean","SPLIT",FACE,{"disambiguationData":[TD([makeQuery(id+"F3.opExtrude","SWEPT_FACE",FACE,{"disambiguationData":[OSD([sQuery(id+"F2.wireOp",EDGE,"E79.trimOffspring")])]})])],"derivedFrom":makeQuery(id+"F1.opExtrude","CAP_FACE",FACE,{"disambiguationData":[OSD([sQuery(id+"F0.wireOp",EDGE,"E0.bottom"),sQuery(id+"F0.wireOp",EDGE,"E0.top"),sQuery(id+"F0.wireOp",EDGE,"E0.left"),sQuery(id+"F0.wireOp",EDGE,"E0.right")])],"isStart":false})});
            chamfer(context, id + "F4", {"entities" : qUnion([Q0, Q1, Q2, Q3, Q4, Q5, Q6, Q7, Q8, Q9, Q10, Q11, Q12, Q13, Q14, Q15, Q16, Q17, Q18, Q19, Q20, Q21, Q22, Q23, Q24, Q25, Q26, Q27, Q28, Q29, Q30, Q31, Q32, Q33, Q34, Q35, Q36, Q37, Q38, Q39, Q40, Q41, Q42, Q43, Q44, Q45, Q46, Q47, Q48, Q49, Q50, Q51, Q52, Q53, Q54, Q55, Q56, Q57, Q58, Q59, Q60, Q61, Q62, Q63, Q64, Q65, Q66, Q67, Q68, Q69, Q70, Q71, Q72, Q73, Q74, Q75, Q76]), "width" : 3.17 * mm});
        }
    });
